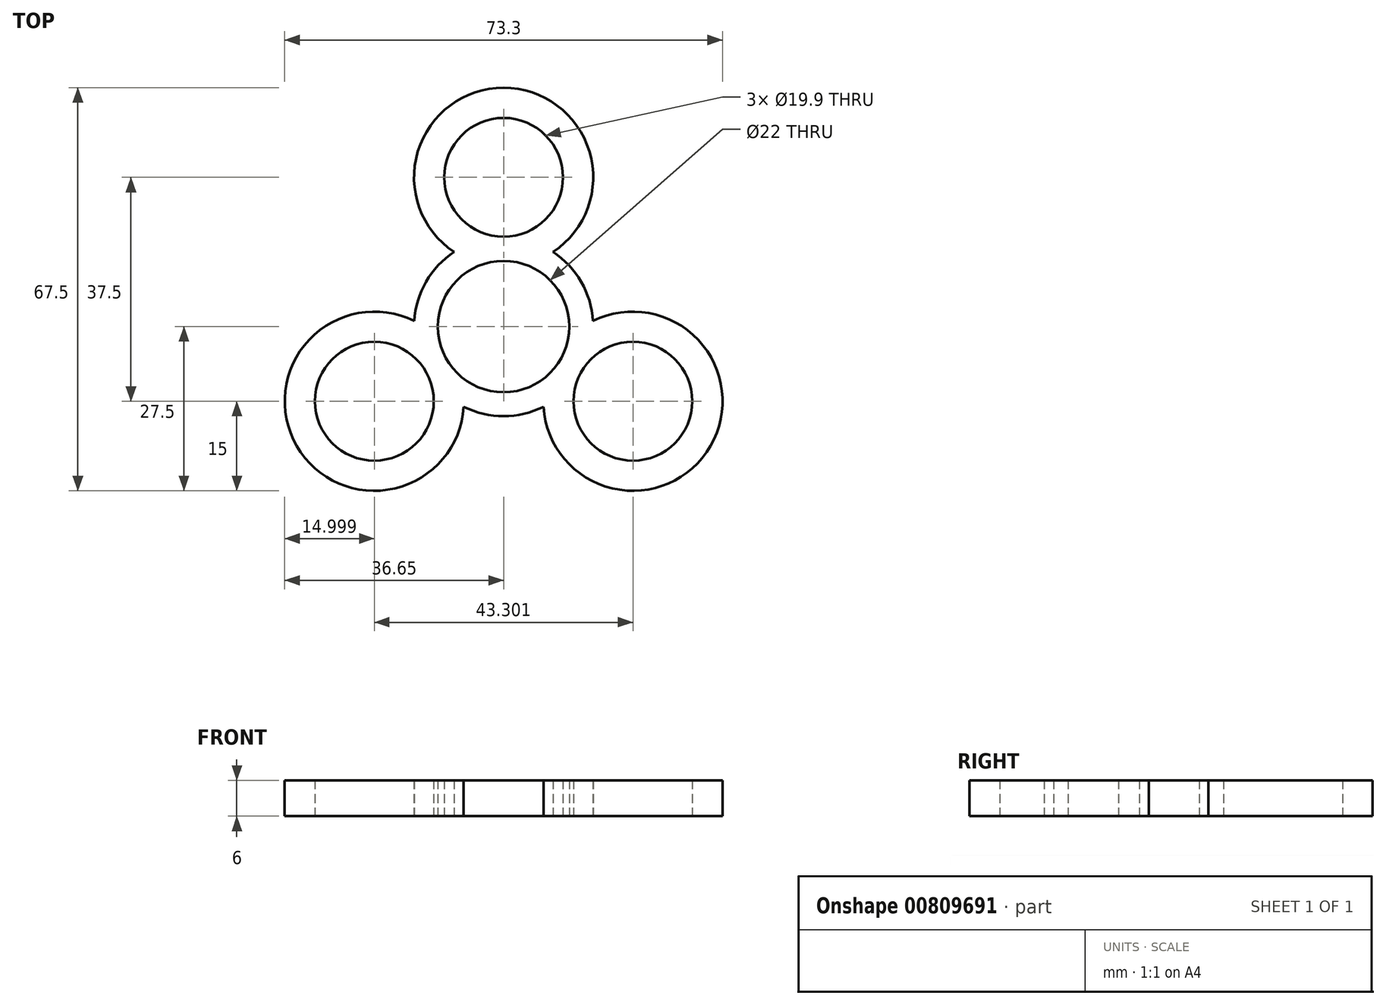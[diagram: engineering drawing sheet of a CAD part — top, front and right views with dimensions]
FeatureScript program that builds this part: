
annotation { "Feature Type Name" : "Feature", "Feature Type Description" : "" }
export const myFeature = defineFeature(function(context is Context, id is Id, definition is map)
    precondition{}
    {
        {
            var Q0;
            Q0=qCreatedBy(makeId("Top.planeOp"),FACE);
            var sketch = newSketch(context, id + "F0", { "sketchPlane" : qUnion([Q0])});
            skArc(sketch, "E0", {"start": v(9.53, 5.5) * mm, "mid": v(0, 11) * mm, "end": v(-9.53, 5.5) * mm});
            skCircle(sketch, "E1", {"center": v(0, 25) * mm, "radius": 9.95 * mm});
            skArc(sketch, "E2", {"start": v(-8.3, 12.5) * mm, "mid": v(-10.93, 10.27) * mm, "end": v(-13, 7.5) * mm});
            skArc(sketch, "E3", {"start": v(8.3, 12.5) * mm, "mid": v(0, 40) * mm, "end": v(-8.3, 12.5) * mm});
            skArc(sketch, "E4.trimOffspring", {"start": v(13, 7.5) * mm, "mid": v(10.93, 10.27) * mm, "end": v(8.3, 12.5) * mm});
            skArc(sketch, "E5.1.0", {"start": v(-14.97, 0.93) * mm, "mid": v(-34.64, -20) * mm, "end": v(-6.68, -13.43) * mm});
            skCircle(sketch, "E5.1.1", {"center": v(-21.65, -12.5) * mm, "radius": 9.95 * mm});
            skArc(sketch, "E5.1.2", {"start": v(-6.68, -13.43) * mm, "mid": v(-3.43, -14.6) * mm, "end": v(0, -15) * mm});
            skArc(sketch, "E5.1.3", {"start": v(-9.53, 5.5) * mm, "mid": v(-9.53, -5.5) * mm, "end": v(0, -11) * mm});
            skArc(sketch, "E5.1.4", {"start": v(-13, 7.5) * mm, "mid": v(-14.36, 4.33) * mm, "end": v(-14.97, 0.93) * mm});
            skArc(sketch, "E5.2.0", {"start": v(6.68, -13.43) * mm, "mid": v(34.64, -20) * mm, "end": v(14.97, 0.93) * mm});
            skCircle(sketch, "E5.2.1", {"center": v(21.65, -12.5) * mm, "radius": 9.95 * mm});
            skArc(sketch, "E5.2.2", {"start": v(14.97, 0.93) * mm, "mid": v(14.36, 4.33) * mm, "end": v(13, 7.5) * mm});
            skArc(sketch, "E5.2.3", {"start": v(0, -11) * mm, "mid": v(9.53, -5.5) * mm, "end": v(9.53, 5.5) * mm});
            skArc(sketch, "E5.2.4", {"start": v(0, -15) * mm, "mid": v(3.43, -14.6) * mm, "end": v(6.68, -13.43) * mm});
            skSolve(sketch);
        }
        {
            var Q0;
            Q0 = qSketchRegion(id + "F0", true);
            extrude(context, id + "F1", {"entities" : qUnion([Q0]), "depth" : 6 * mm, "offsetDistance" : 25 * mm});
        }
    });
